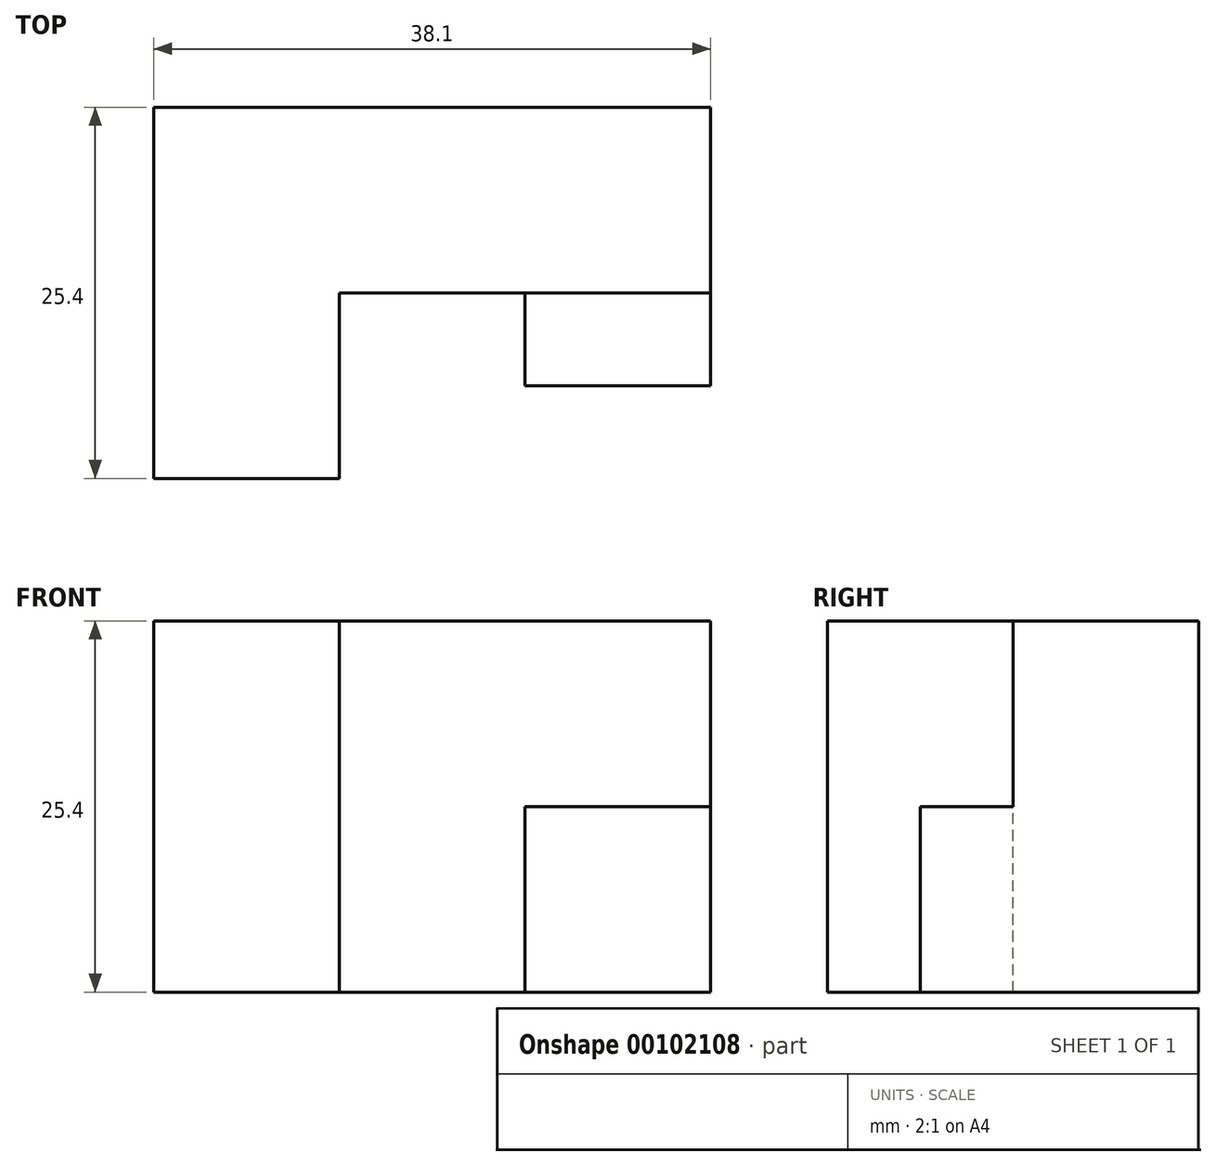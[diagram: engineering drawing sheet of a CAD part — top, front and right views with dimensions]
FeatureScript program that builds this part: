
annotation { "Feature Type Name" : "Feature", "Feature Type Description" : "" }
export const myFeature = defineFeature(function(context is Context, id is Id, definition is map)
    precondition{}
    {
        {
            var Q0;
            Q0=qCreatedBy(makeId("Front.planeOp"),FACE);
            var sketch = newSketch(context, id + "F0", { "sketchPlane" : qUnion([Q0])});
            skLineSegment(sketch, "E0.bottom", {"start": v(0, 0) * mm, "end": v(38.1, 0) * mm});
            skLineSegment(sketch, "E0.top", {"start": v(0, 25.4) * mm, "end": v(38.1, 25.4) * mm});
            skLineSegment(sketch, "E0.left", {"start": v(0, 0) * mm, "end": v(0, 25.4) * mm});
            skLineSegment(sketch, "E0.right", {"start": v(38.1, 0) * mm, "end": v(38.1, 25.4) * mm});
            skSolve(sketch);
        }
        {
            var Q0;
            Q0 = qSketchRegion(id + "F0", true);
            extrude(context, id + "F1", {"entities" : qUnion([Q0]), "oppositeDirection" : true, "depth" : 12.7 * mm});
        }
        {
            var Q0;
            Q0=qCreatedBy(makeId("Front.planeOp"),FACE);
            var sketch = newSketch(context, id + "F2", { "sketchPlane" : qUnion([Q0])});
            skLineSegment(sketch, "E1.bottom", {"start": v(0, 0) * mm, "end": v(12.7, 0) * mm});
            skLineSegment(sketch, "E1.top", {"start": v(0, 25.4) * mm, "end": v(12.7, 25.4) * mm});
            skLineSegment(sketch, "E1.left", {"start": v(0, 0) * mm, "end": v(0, 25.4) * mm});
            skLineSegment(sketch, "E1.right", {"start": v(12.7, 0) * mm, "end": v(12.7, 25.4) * mm});
            skSolve(sketch);
        }
        {
            var Q0;
            Q0 = qSketchRegion(id + "F2", true);
            extrude(context, id + "F3", {"entities" : qUnion([Q0]), "operationType" : NewBodyOperationType.ADD, "depth" : 12.7 * mm});
        }
        {
            var Q0;
            Q0=makeQuery(id+"F1.opExtrude","CAP_FACE",FACE,{"disambiguationData":[OSD([sQuery(id+"F0.wireOp",EDGE,"E0.bottom"),sQuery(id+"F0.wireOp",EDGE,"E0.top"),sQuery(id+"F0.wireOp",EDGE,"E0.left"),sQuery(id+"F0.wireOp",EDGE,"E0.right")])],"isStart":true});
            var sketch = newSketch(context, id + "F4", { "sketchPlane" : qUnion([Q0])});
            skLineSegment(sketch, "E2.bottom", {"start": v(38.1, 0) * mm, "end": v(25.4, 0) * mm});
            skLineSegment(sketch, "E2.top", {"start": v(38.1, 12.7) * mm, "end": v(25.4, 12.7) * mm});
            skLineSegment(sketch, "E2.left", {"start": v(38.1, 0) * mm, "end": v(38.1, 12.7) * mm});
            skLineSegment(sketch, "E2.right", {"start": v(25.4, 0) * mm, "end": v(25.4, 12.7) * mm});
            skSolve(sketch);
        }
        {
            var Q0;
            Q0 = qSketchRegion(id + "F4", true);
            extrude(context, id + "F5", {"entities" : qUnion([Q0]), "operationType" : NewBodyOperationType.ADD, "depth" : 6.35 * mm});
        }
    });
